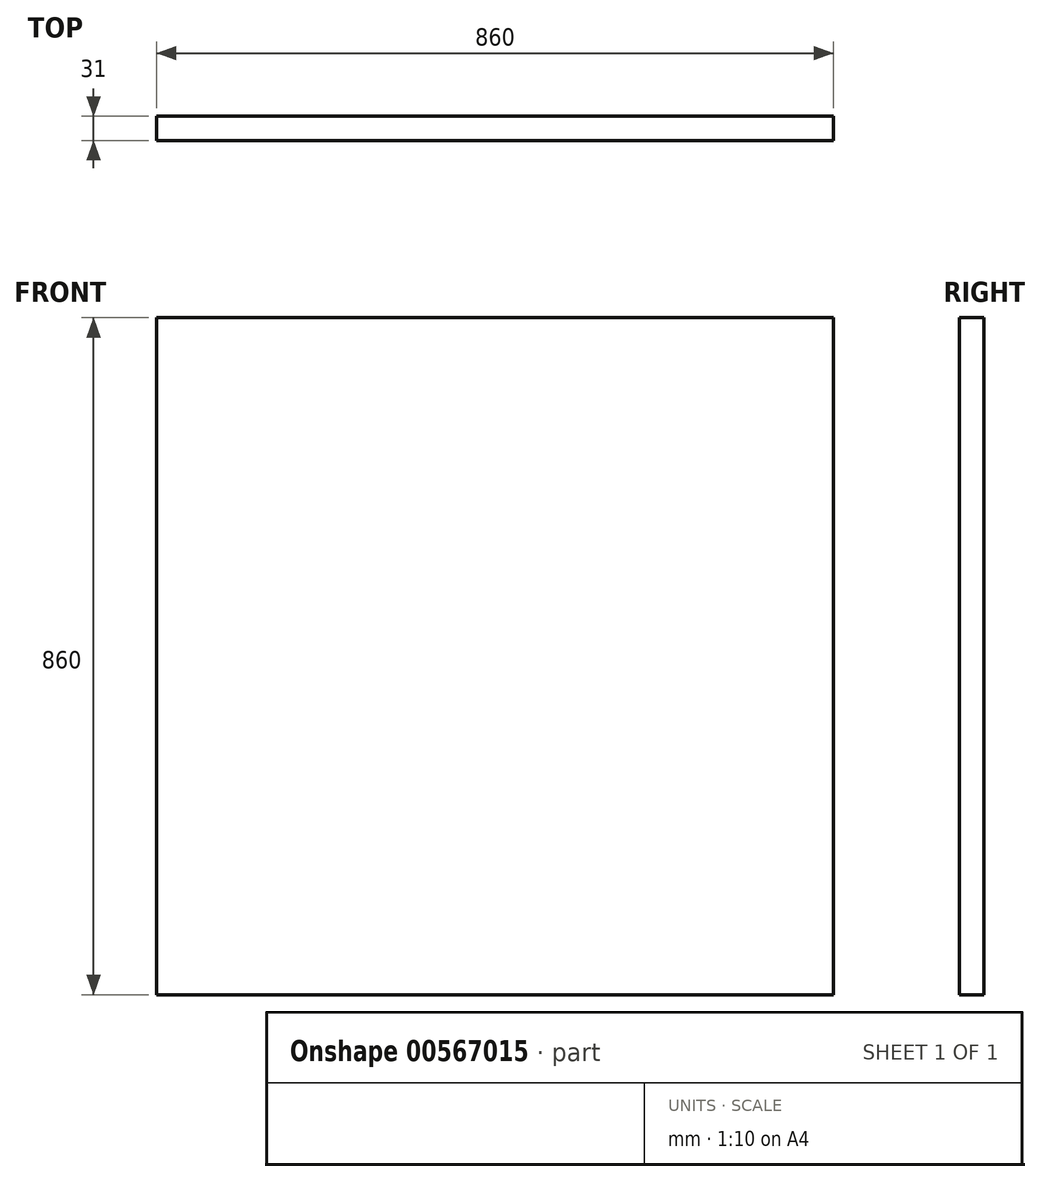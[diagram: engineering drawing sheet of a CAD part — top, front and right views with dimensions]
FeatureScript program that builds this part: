
annotation { "Feature Type Name" : "Feature", "Feature Type Description" : "" }
export const myFeature = defineFeature(function(context is Context, id is Id, definition is map)
    precondition{}
    {
        {
            var Q0;
            Q0=qCreatedBy(makeId("Front.planeOp"),FACE);
            var sketch = newSketch(context, id + "F0", { "sketchPlane" : qUnion([Q0])});
            skLineSegment(sketch, "E0.bottom", {"start": v(-455.41, 708.62) * mm, "end": v(404.59, 708.62) * mm});
            skLineSegment(sketch, "E0.top", {"start": v(-455.41, -151.38) * mm, "end": v(404.59, -151.38) * mm});
            skLineSegment(sketch, "E0.left", {"start": v(-455.41, 708.62) * mm, "end": v(-455.41, -151.38) * mm});
            skLineSegment(sketch, "E0.right", {"start": v(404.59, 708.62) * mm, "end": v(404.59, -151.38) * mm});
            skSolve(sketch);
        }
        {
            var Q0;
            Q0 = qSketchRegion(id + "F0", true);
            extrude(context, id + "F1", {"entities" : qUnion([Q0]), "depth" : 31 * mm, "offsetDistance" : 25 * mm});
        }
    });
